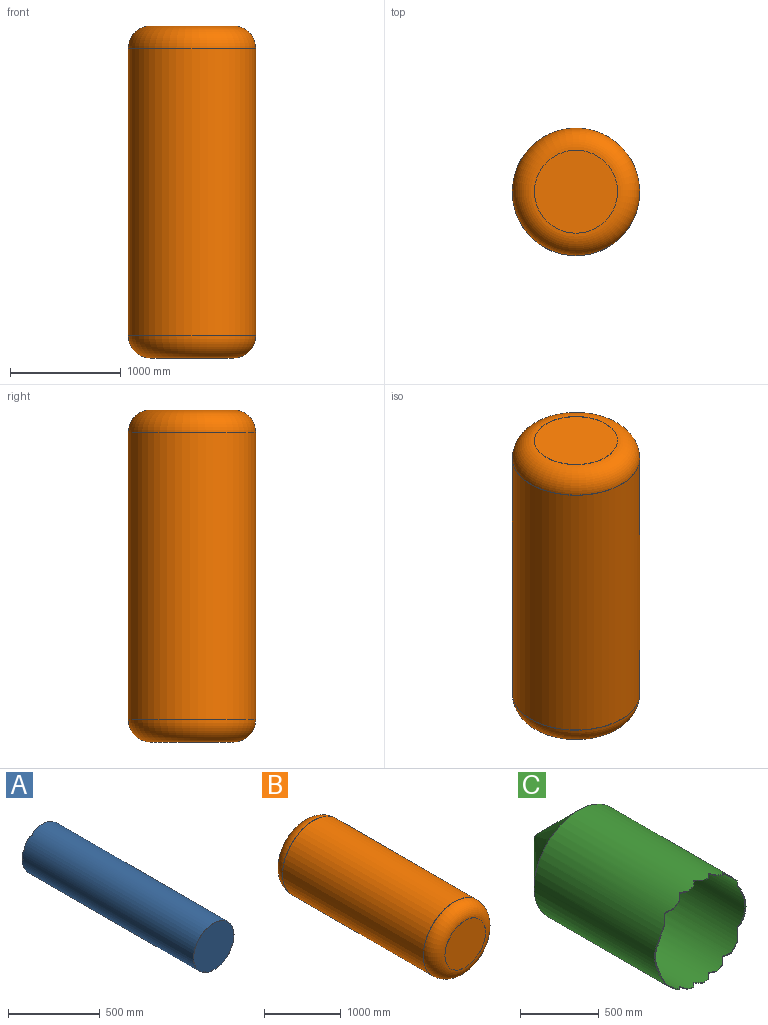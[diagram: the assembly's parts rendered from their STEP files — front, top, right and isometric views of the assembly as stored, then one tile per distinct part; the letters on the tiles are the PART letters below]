
ASSEMBLY  parts=3 mates=2
PART A: 34 faces, bbox 311.7x1322.5x311.7 mm
  f0: plane 10.01x10.01mm, normal (0,0.71,-0.71), area 35.4mm2, adj f17,f20,f23,f32
  f1: plane 10.01x10.01mm, normal (0,0.71,0.71), area 35.4mm2, adj f13,f20,f22,f32
  f2: plane 10x10mm, normal (0,0.71,-0.71), area 39mm2, adj f15,f20,f25,f32
  f3: plane 10x10mm, normal (0,0.71,0.71), area 37.8mm2, adj f18,f20,f24,f32
  f4: plane 18.1x10mm, normal (0,0.71,0.71), area 60.3mm2, adj f16,f20,f27,f32
  f5: plane 23.38x10mm, normal (0,0.71,-0.71), area 73.2mm2, adj f14,f20,f26,f32
  f6: plane 10x10mm, normal (0,0.71,0.71), area 39mm2, adj f10,f20,f29,f32
  f7: plane 10x10mm, normal (0,0.71,-0.71), area 37.8mm2, adj f13,f20,f28,f32
  f8: plane 23.38x10mm, normal (0,0.71,0.71), area 73.2mm2, adj f19,f20,f31,f32
  f9: plane 18.1x10mm, normal (0,0.71,-0.71), area 60.3mm2, adj f11,f20,f30,f32
  f10: plane 50x43.77mm, normal (0,1,0), area 161.8mm2, adj f6,f20,f31,f32
  f11: plane 50x43.77mm, normal (0,1,0), area 161.8mm2, adj f9,f20,f28,f32
  f12: plane 40x10.56mm, normal (0,1,0), area 102.3mm2, adj f20,f23,f29,f32
  f13: plane 40x10.56mm, normal (0,1,0), area 102.3mm2, adj f1,f7,f20,f32
  f14: plane 136.95x15.85mm, normal (0,1,0), area 338.6mm2, adj f5,f20,f27,f32
  f15: plane 50x43.77mm, normal (0,1,0), area 161.8mm2, adj f2,f20,f26,f32
  f16: plane 50x43.77mm, normal (0,1,0), area 161.8mm2, adj f4,f20,f24,f32
  f17: plane 40x10.56mm, normal (0,1,0), area 102.3mm2, adj f0,f20,f25,f32
  f18: plane 40x10.56mm, normal (0,1,0), area 102.3mm2, adj f3,f20,f22,f32
  f19: plane 136.95x15.85mm, normal (0,1,0), area 338.6mm2, adj f8,f20,f30,f32
  f20: cylinder r=153.35mm len=1320mm, axis (0,1,0), area 1270451.4mm2, adj f0,f1,f2,f3,f4,f5,f6,f7
  f21: plane 306.7x306.7mm, normal (0,1,0), area 73877.7mm2, adj f20
  f22: plane 10.01x10.01mm, normal (0,0.71,-0.71), area 35.4mm2, adj f1,f18,f20,f32
  f23: plane 10.01x10.01mm, normal (0,0.71,0.71), area 35.4mm2, adj f0,f12,f20,f32
  f24: plane 10x10mm, normal (0,0.71,-0.71), area 39mm2, adj f3,f16,f20,f32
  f25: plane 10x10mm, normal (0,0.71,0.71), area 37.8mm2, adj f2,f17,f20,f32
  f26: plane 18.1x10mm, normal (0,0.71,0.71), area 60.3mm2, adj f5,f15,f20,f32
  f27: plane 23.38x10mm, normal (0,0.71,-0.71), area 73.2mm2, adj f4,f14,f20,f32
  f28: plane 10x10mm, normal (0,0.71,0.71), area 39mm2, adj f7,f11,f20,f32
  f29: plane 10x10mm, normal (0,0.71,-0.71), area 37.8mm2, adj f6,f12,f20,f32
  f30: plane 23.38x10mm, normal (0,0.71,0.71), area 73.2mm2, adj f9,f19,f20,f32
  f31: plane 18.1x10mm, normal (0,0.71,-0.71), area 60.3mm2, adj f8,f10,f20,f32
  f32: cylinder r=155.85mm len=1322.5mm, axis (0,1,0), area 1293666.2mm2, adj f0,f1,f2,f3,f4,f5,f6,f7
  f33: plane 311.7x311.7mm, normal (0,-1,0), area 76306.2mm2, adj f32
PART B: 11 faces, bbox 1244.8x3000x1244.8 mm
  f0: cylinder r=575mm len=2600mm, axis (0,1,0), area 9393362mm2, adj f3,f4
  f1: plane 750x750mm, normal (0,1,0), area 334635.3mm2, adj f4,f5
  f2: plane 750x750mm, normal (0,-1,0), area 441786.5mm2, adj f3
  f3: torus R=375mm, axis (0,-1,0), area 991547.7mm2, adj f0,f2
  f4: torus R=375mm, axis (0,-1,0), area 991547.7mm2, adj f0,f1
  f5: cylinder r=184.68mm len=369.36mm, axis (0,1,0), area 2901mm2, adj f1,f7
  f6: cylinder r=572.5mm len=2600mm, axis (0,1,0), area 9352521.3mm2, adj f9,f10
  f7: plane 750x750mm, normal (0,-1,0), area 334635.3mm2, adj f5,f10
  f8: plane 750x750mm, normal (0,1,0), area 441786.5mm2, adj f9
  f9: torus R=375mm, axis (0,-1,0), area 976051.1mm2, adj f6,f8
  f10: torus R=375mm, axis (0,-1,0), area 976051.1mm2, adj f6,f7
PART C: 41 faces, bbox 800.4x1470.4x800.4 mm
  f0: plane 44.06x40mm, normal (-0.71,-0.71,0), area 386.5mm2, adj f13,f19,f22,f39
  f1: plane 58.42x40mm, normal (0.71,-0.71,0), area 454.7mm2, adj f19,f21,f36,f39
  f2: plane 40.41x40.41mm, normal (-0.71,-0.71,0), area 302.4mm2, adj f12,f19,f24,f39
  f3: plane 40x40mm, normal (0.71,-0.71,0), area 317.5mm2, adj f19,f23,f35,f39
  f4: plane 40.03x40.03mm, normal (-0.71,-0.71,0), area 283.1mm2, adj f19,f26,f33,f39
  f5: plane 40.13x40.13mm, normal (0.71,-0.71,0), area 285.2mm2, adj f19,f25,f34,f39
  f6: plane 40.34x40.34mm, normal (-0.71,-0.71,0), area 296.9mm2, adj f19,f28,f38,f39
  f7: plane 40.21x40.21mm, normal (0.71,-0.71,0), area 288.9mm2, adj f11,f19,f27,f39
  f8: plane 40x40mm, normal (-0.71,-0.71,0), area 364.6mm2, adj f19,f30,f37,f39
  f9: plane 40x40mm, normal (0.71,-0.71,0), area 333.6mm2, adj f16,f19,f29,f39
  f10: plane 77.44x40mm, normal (0.71,-0.71,0), area 554.4mm2, adj f15,f19,f31,f39
  f11: plane 50x9.46mm, normal (0,-1,0), area 251.1mm2, adj f7,f19,f25,f39
  f12: plane 50x17.5mm, normal (0,-1,0), area 257.7mm2, adj f2,f19,f26,f39
  f13: plane 50x40.59mm, normal (0,-1,0), area 304mm2, adj f0,f19,f24,f39
  f14: plane 118.23x50mm, normal (0,-1,0), area 583.8mm2, adj f19,f20,f22,f39
  f15: plane 63.56x50mm, normal (0,-1,0), area 375.6mm2, adj f10,f19,f29,f39
  f16: plane 50x28.4mm, normal (0,-1,0), area 275.2mm2, adj f9,f19,f27,f39
  f17: cone r=396.46mm half-angle=45deg, axis (0,-1,0), area 689202.2mm2, adj f19,f40
  f18: cone r=400mm half-angle=45deg, axis (0,-1,0), area 706862.7mm2, adj f39,f40
  f19: cylinder r=395mm len=1097.93mm, axis (0,-1,0), area 2695004.7mm2, adj f0,f1,f2,f3,f4,f5,f6,f7
  f20: plane 249.8x20mm, normal (-0.71,-0.71,0), area 1673mm2, adj f14,f19,f36,f39
  f21: plane 44.06x40mm, normal (-0.71,-0.71,0), area 386.5mm2, adj f1,f19,f35,f39
  f22: plane 58.42x40mm, normal (0.71,-0.71,0), area 454.7mm2, adj f0,f14,f19,f39
  f23: plane 40.41x40.41mm, normal (-0.71,-0.71,0), area 302.4mm2, adj f3,f19,f34,f39
  f24: plane 40x40mm, normal (0.71,-0.71,0), area 317.5mm2, adj f2,f13,f19,f39
  f25: plane 40.02x40.02mm, normal (-0.71,-0.71,0), area 283.1mm2, adj f5,f11,f19,f39
  f26: plane 40.13x40.13mm, normal (0.71,-0.71,0), area 285.2mm2, adj f4,f12,f19,f39
  f27: plane 40.34x40.34mm, normal (-0.71,-0.71,0), area 296.9mm2, adj f7,f16,f19,f39
  f28: plane 40.21x40.21mm, normal (0.71,-0.71,0), area 288.9mm2, adj f6,f19,f33,f39
  f29: plane 40x40mm, normal (-0.71,-0.71,0), area 364.6mm2, adj f9,f15,f19,f39
  f30: plane 40x40mm, normal (0.71,-0.71,0), area 333.6mm2, adj f8,f19,f38,f39
  f31: plane 348.71x40mm, normal (-0.71,-0.71,0), area 2461.1mm2, adj f10,f19,f32,f39
  f32: plane 77.44x40mm, normal (0.71,-0.71,0), area 554.4mm2, adj f19,f31,f37,f39
  f33: plane 50x9.46mm, normal (0,-1,0), area 251.1mm2, adj f4,f19,f28,f39
  f34: plane 50x17.5mm, normal (0,-1,0), area 257.7mm2, adj f5,f19,f23,f39
  f35: plane 50x40.59mm, normal (0,-1,0), area 304mm2, adj f3,f19,f21,f39
  f36: plane 118.23x50mm, normal (0,-1,0), area 583.8mm2, adj f1,f19,f20,f39
  f37: plane 63.56x50mm, normal (0,-1,0), area 375.6mm2, adj f8,f19,f32,f39
  f38: plane 50x28.4mm, normal (0,-1,0), area 275.2mm2, adj f6,f19,f30,f39
  f39: cylinder r=400mm len=1100mm, axis (0,-1,0), area 2734510.4mm2, adj f0,f1,f2,f3,f4,f5,f6,f7
  f40: cylinder r=30mm len=60mm, axis (0,1,0), area 1332.9mm2, adj f17,f18
PLACE A rot(axis=(1,0,0),90deg) t=(-5.85,0,-1527.5)mm
PLACE B rot(axis=(-1,0,0),90deg) t=(0,0,-3000)mm
PLACE C rot(axis=(-1,0,0),90deg) t=(0,0,-1530)mm
MATE fastened A.f20 <-> C.f17  axis (0,0,-1) through (0,0,-2850)mm
MATE fastened B.f0 <-> C.f17  axis (0,0,-1) through (0,0,-3000)mm
